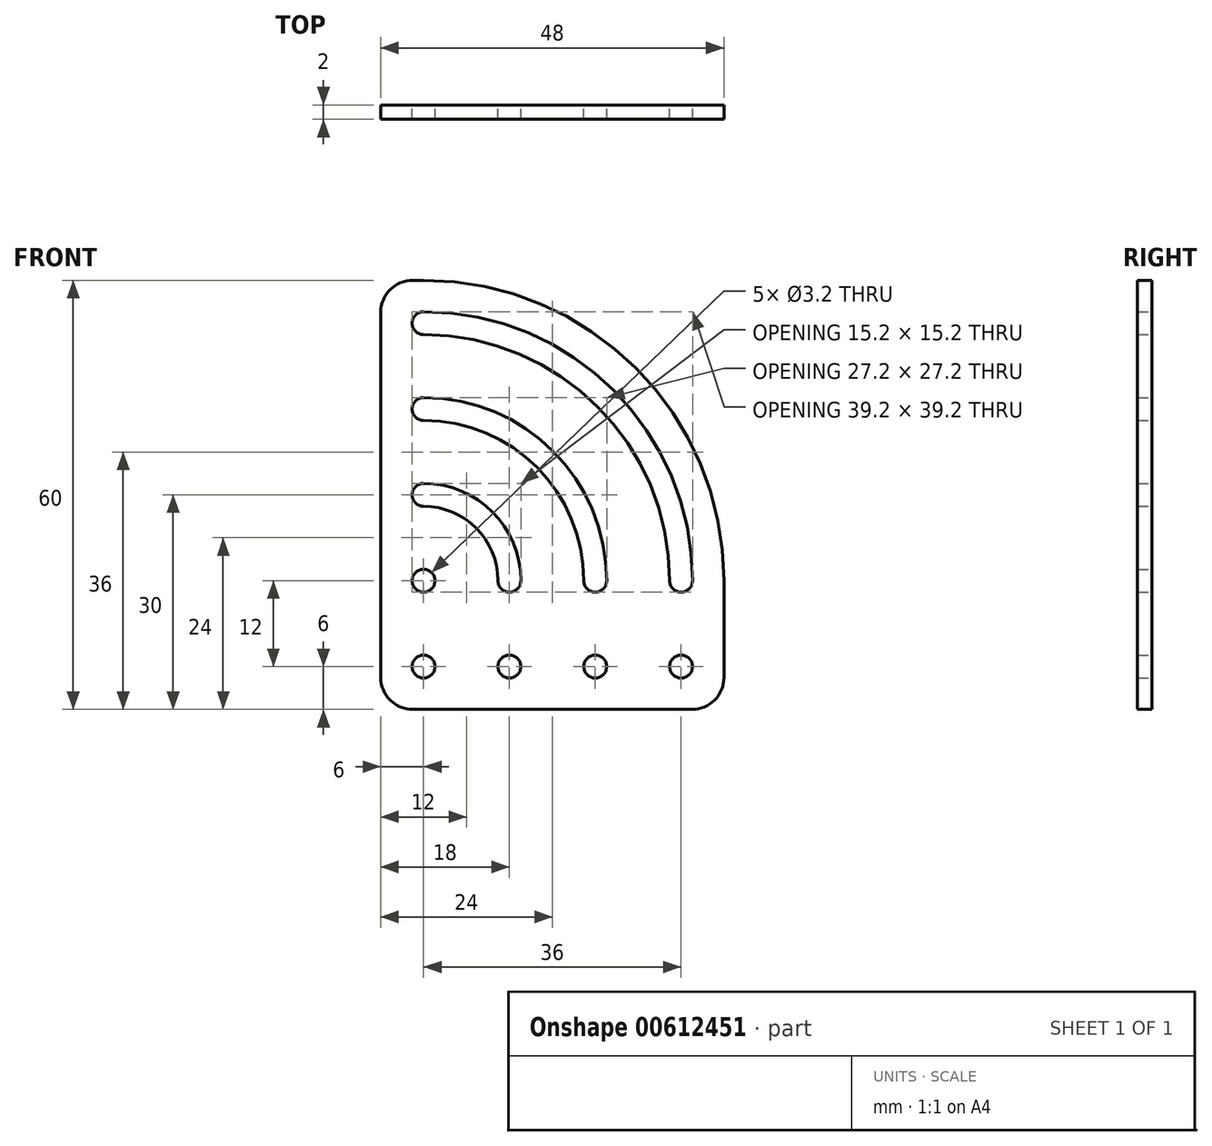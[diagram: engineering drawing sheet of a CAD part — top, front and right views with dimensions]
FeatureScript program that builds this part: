
annotation { "Feature Type Name" : "Feature", "Feature Type Description" : "" }
export const myFeature = defineFeature(function(context is Context, id is Id, definition is map)
    precondition{}
    {
        {
            var Q0;
            Q0=qCreatedBy(makeId("Front.planeOp"),FACE);
            var sketch = newSketch(context, id + "F0", { "sketchPlane" : qUnion([Q0])});
            skLineSegment(sketch, "E0.bottom", {"start": v(4.5, 0) * mm, "end": v(43.5, 0) * mm});
            skLineSegment(sketch, "E0.top", {"start": v(4.5, 60) * mm, "end": v(6, 60) * mm});
            skLineSegment(sketch, "E0.left", {"start": v(0, 4.5) * mm, "end": v(0, 55.5) * mm});
            skLineSegment(sketch, "E0.right", {"start": v(48, 4.5) * mm, "end": v(48, 18) * mm});
            skCircle(sketch, "E1", {"center": v(6, 6) * mm, "radius": 1.6 * mm});
            skCircle(sketch, "E2", {"center": v(18, 6) * mm, "radius": 1.6 * mm});
            skCircle(sketch, "E3", {"center": v(42, 6) * mm, "radius": 1.6 * mm});
            skCircle(sketch, "E4", {"center": v(30, 6) * mm, "radius": 1.6 * mm});
            skCircle(sketch, "E5", {"center": v(6, 18) * mm, "radius": 1.6 * mm});
            skArc(sketch, "E6", {"start": v(6, 30) * mm, "mid": v(14.49, 26.49) * mm, "end": v(18, 18) * mm, "construction": true});
            skArc(sketch, "E7", {"start": v(6, 42) * mm, "mid": v(22.97, 34.97) * mm, "end": v(30, 18) * mm, "construction": true});
            skArc(sketch, "E8", {"start": v(6, 54) * mm, "mid": v(31.46, 43.46) * mm, "end": v(42, 18) * mm, "construction": true});
            skArc(sketch, "E9", {"start": v(48, 18) * mm, "mid": v(35.7, 47.7) * mm, "end": v(6, 60) * mm});
            skArc(sketch, "E10.0.startCap", {"start": v(6, 28.4) * mm, "mid": v(4.4, 30) * mm, "end": v(6, 31.6) * mm});
            skArc(sketch, "E10.0.endCap", {"start": v(19.6, 18) * mm, "mid": v(18, 16.4) * mm, "end": v(16.4, 18) * mm});
            skArc(sketch, "E10.0.left", {"start": v(6, 31.6) * mm, "mid": v(15.62, 27.62) * mm, "end": v(19.6, 18) * mm});
            skArc(sketch, "E10.0.right", {"start": v(6, 28.4) * mm, "mid": v(13.35, 25.35) * mm, "end": v(16.4, 18) * mm});
            skArc(sketch, "E11.0.startCap", {"start": v(6, 40.4) * mm, "mid": v(4.4, 42) * mm, "end": v(6, 43.6) * mm});
            skArc(sketch, "E11.0.endCap", {"start": v(31.6, 18) * mm, "mid": v(30, 16.4) * mm, "end": v(28.4, 18) * mm});
            skArc(sketch, "E11.0.left", {"start": v(6, 43.6) * mm, "mid": v(24.1, 36.1) * mm, "end": v(31.6, 18) * mm});
            skArc(sketch, "E11.0.right", {"start": v(6, 40.4) * mm, "mid": v(21.84, 33.84) * mm, "end": v(28.4, 18) * mm});
            skArc(sketch, "E11.1.startCap", {"start": v(6, 52.4) * mm, "mid": v(4.4, 54) * mm, "end": v(6, 55.6) * mm});
            skArc(sketch, "E11.1.endCap", {"start": v(43.6, 18) * mm, "mid": v(42, 16.4) * mm, "end": v(40.4, 18) * mm});
            skArc(sketch, "E11.1.left", {"start": v(6, 55.6) * mm, "mid": v(32.59, 44.59) * mm, "end": v(43.6, 18) * mm});
            skArc(sketch, "E11.1.right", {"start": v(6, 52.4) * mm, "mid": v(30.32, 42.32) * mm, "end": v(40.4, 18) * mm});
            skPoint(sketch, "E12.visualSharp", {"position": v(48, 0) * mm});
            skArc(sketch, "E12.filletArc", {"start": v(43.5, 0) * mm, "mid": v(46.68, 1.32) * mm, "end": v(48, 4.5) * mm});
            skPoint(sketch, "E13.visualSharp", {"position": v(0, 60) * mm});
            skArc(sketch, "E13.filletArc", {"start": v(4.5, 60) * mm, "mid": v(1.32, 58.68) * mm, "end": v(0, 55.5) * mm});
            skPoint(sketch, "E14.visualSharp", {"position": v(0, 0) * mm});
            skArc(sketch, "E14.filletArc", {"start": v(0, 4.5) * mm, "mid": v(1.32, 1.32) * mm, "end": v(4.5, 0) * mm});
            skSolve(sketch);
        }
        {
            var Q0;
            Q0=makeQuery(id+"F0.imprint","IMPRINT",FACE,{"disambiguationData":[TD([[makeQuery(id+"F0.imprint","IMPRINT",EDGE,{"derivedFrom":sQuery(id+"F0.wireOp",EDGE,"E0.bottom")}),1.0]])]});
            extrude(context, id + "F1", {"entities" : qUnion([Q0]), "depth" : 2 * mm, "offsetDistance" : 25 * mm});
        }
    });
